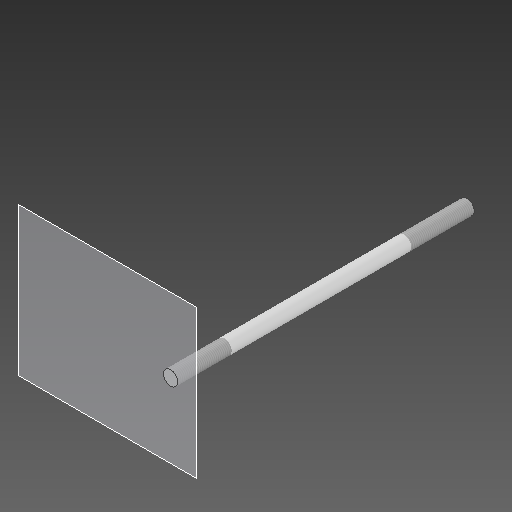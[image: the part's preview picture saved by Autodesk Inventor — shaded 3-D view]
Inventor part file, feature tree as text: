
AUTODESK INVENTOR PART (.ipt)
format: ipt  version: 2021 (Build 250183000, 183)  size: 84,480 bytes
history: native  units: in
note: dims shown in document units (in); Inventor stores cm internally (conversion verified against a paired STEP export)
features: other x3, sketch x1, plane x1
ambient origin geometry x8: Origin, YZ Plane, XZ Plane, XY Plane, X Axis, Y Axis, Z Axis, Center Point
bodies: Solid1 (feature_tree)
feature tree (5):
  other  "Eje roscado base soporte tubo_MIR.ipt"
  other  "Solid1::Eje roscado base soporte tubo_MIR.ipt"
  other  "TaggingFeature1"
  sketch  "Sketch1"  dims[d0=0.3937in]
  plane  "Work Plane1"
